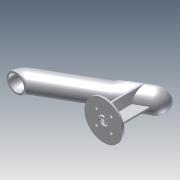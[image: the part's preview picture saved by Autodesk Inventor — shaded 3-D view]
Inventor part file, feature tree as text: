
AUTODESK INVENTOR PART (.ipt)
format: ipt  version: 2011 (Build 150239000, 239)  size: 264,704 bytes
history: native  units: mm
features: other x15, sketch x12, extrude x7, loft x2, sweep x1
ambient origin geometry x8: Origin, YZ Plane, XZ Plane, XY Plane, X Axis, Y Axis, Z Axis, Center Point
bodies: Solid1 (feature_tree)
feature tree (37):
  other  "Skelethon sketch"
  extrude  "wheel extr"  Depth=45.0mm
  other  "Tube Ref plane"
  other  "Tube ut_Ref Plane"
  other  "Tube ut_ProfileRef Plane"
  other  "Tube ut_profileRef Plane2"
  sketch  "Sketch4"  dims[d2=37.0mm d3=9.0mm]
  other  "Tube ut_profileRef Plane3"
  sketch  "Sketch6"  dims[d4=45.0deg d5=10.0mm]
  sketch  "Sketch7"  dims[d6=3.0mm d7=40.0mm d9=360.0deg]
  sketch  "Sketch8"  dims[d11=1.75mm d12=0.0mm]
  loft  "middle loft transition"
  loft  "middle loft transcut"
  extrude  "catch tube solid"  Depth=40.0mm TaperAngle=360.0deg
  extrude  "exit tube solid "  TaperAngle=0.0deg  [1 undecoded]
  other  "cut height ref sketch"
  extrude  "catch tube solid cut"  Depth=15.0mm
  extrude  "tube support"  Depth=1.75mm
  other  "exit endcap top"
  other  "exit  endcap plane"
  other  "exit encap sketch"
  sweep  "exit encap"
  other  "catch tube open plane"
  other  "top endcap"
  extrude  "top endcap cut"  TaperAngle=0.0deg  [1 undecoded]
  other  "exit tube checking plane"
  extrude  "exit tube checking cut"  TaperAngle=0.0deg  [1 undecoded]
  other  "print ref plane"
  other  "print split"
  sketch  "Sketch2"  dims[d0=30.0deg d1=45.0mm]
  sketch  "Sketch10"  dims[d13=11.0mm d17=15.0mm]
  sketch  "Sketch11"  dims[d19=-3.75mm d20=1.75mm]
  sketch  "Sketch13"  dims[d21=-11.25mm d22=20.25mm]
  sketch  "Sketch14"  dims[d23=1.75mm d30=0.0mm d31=90.0deg]
  sketch  "Sketch32"  dims[d32=0.0mm d33=90.0deg d34=0.0mm d35=90.0deg]
  sketch  "Sketch33"  dims[d36=0.0mm d37=90.0deg]
  sketch  "Sketch34"  dims[d38=10.0mm d39=0.0mm d40=10.0mm d41=0.0mm d42=10.875mm d44=0.0mm d45=0.0mm d46=1.75mm d47=10.0mm d48=0.0mm d65=1.75mm d66=15.0mm d67=15.0mm d73=180.0deg d76=30.0mm d77=30.0mm d78=0.0mm d80=30.0mm d81=0.0mm d82=5.0mm d83=0.0mm d84=10.0mm d85=0.0mm d86=3.5mm d87=-10.975mm]
note: 3 required parameter values undecoded (feature->parameter linkage not recoverable at this tier; creation-order binding heuristic only, values carry confidence <= 0.55)
